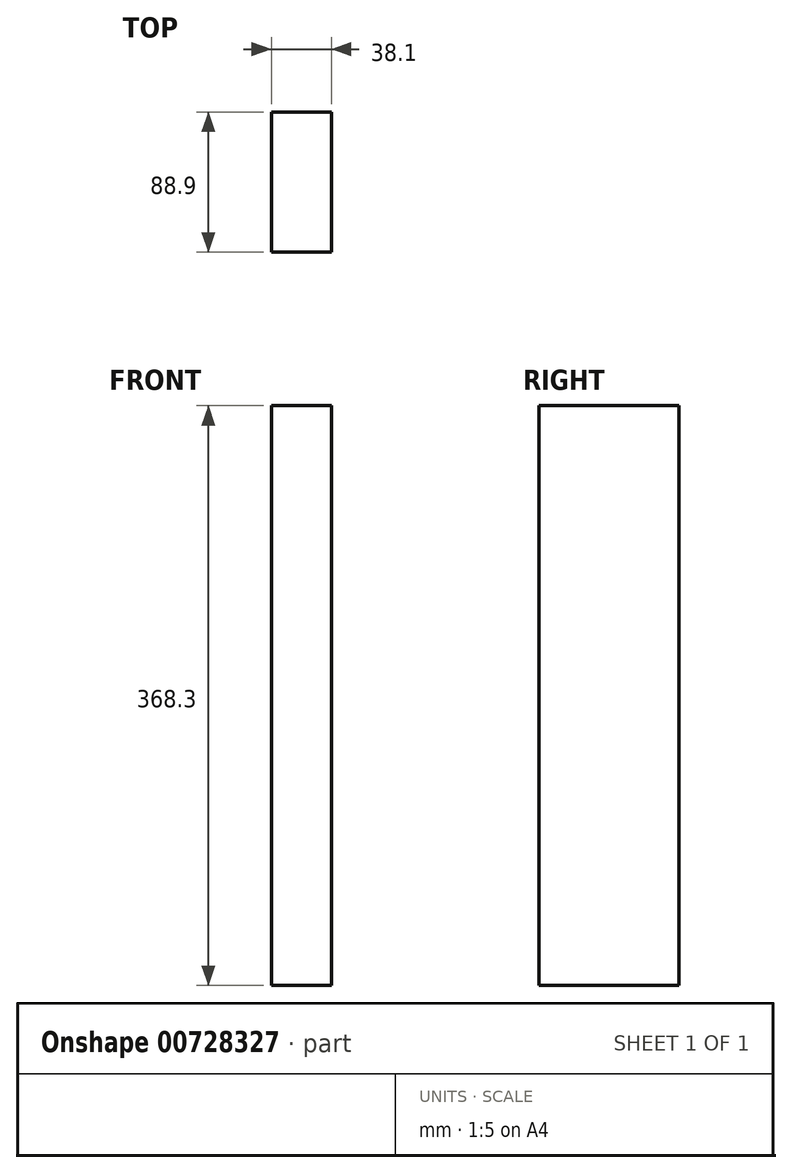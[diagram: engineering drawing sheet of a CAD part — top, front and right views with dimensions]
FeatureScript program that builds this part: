
annotation { "Feature Type Name" : "Feature", "Feature Type Description" : "" }
export const myFeature = defineFeature(function(context is Context, id is Id, definition is map)
    precondition{}
    {
        {
            var Q0;
            Q0=qCreatedBy(makeId("Front.planeOp"),FACE);
            var sketch = newSketch(context, id + "F0", { "sketchPlane" : qUnion([Q0])});
            skLineSegment(sketch, "E0.bottom", {"start": v(-67.87, -188.61) * mm, "end": v(-29.77, -188.61) * mm});
            skLineSegment(sketch, "E0.top", {"start": v(-67.87, 179.69) * mm, "end": v(-29.77, 179.69) * mm});
            skLineSegment(sketch, "E0.left", {"start": v(-67.87, -188.61) * mm, "end": v(-67.87, 179.69) * mm});
            skLineSegment(sketch, "E0.right", {"start": v(-29.77, -188.61) * mm, "end": v(-29.77, 179.69) * mm});
            skSolve(sketch);
        }
        {
            var Q0;
            Q0=qSketchRegion(id+"F0",true);
            extrude(context, id + "F1", {"entities" : qUnion([Q0]), "depth" : 88.9 * mm, "offsetDistance" : 25.4 * mm});
        }
    });
